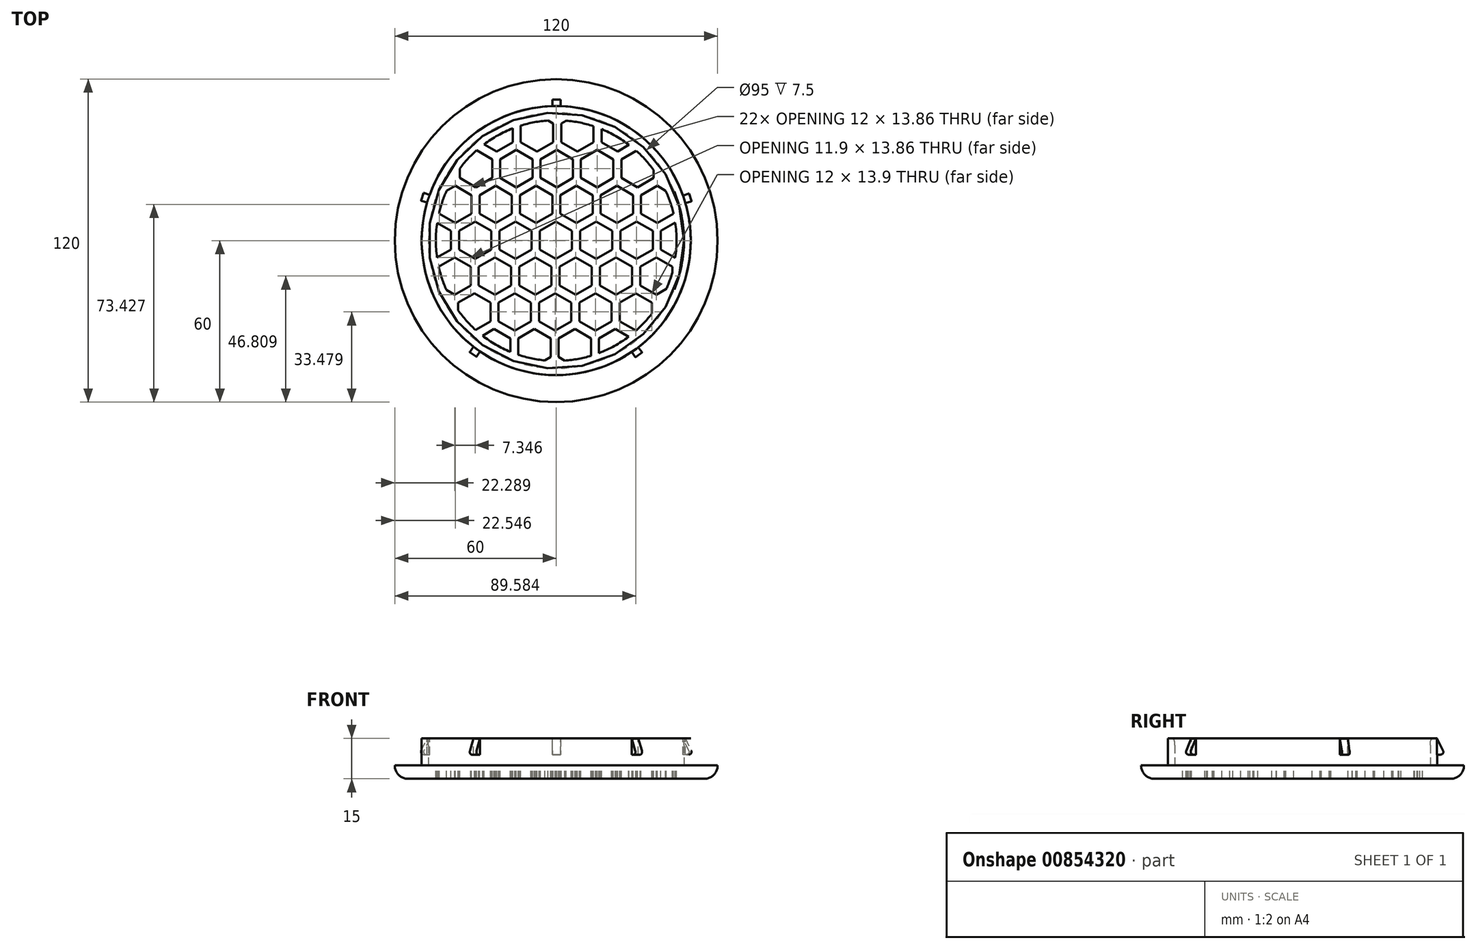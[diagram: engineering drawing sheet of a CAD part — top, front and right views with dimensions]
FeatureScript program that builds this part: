
annotation { "Feature Type Name" : "Feature", "Feature Type Description" : "" }
export const myFeature = defineFeature(function(context is Context, id is Id, definition is map)
    precondition{}
    {
        {
            var Q0;
            Q0=qCreatedBy(makeId("Top.planeOp"),FACE);
            var sketch = newSketch(context, id + "F0", { "sketchPlane" : qUnion([Q0])});
            skCircle(sketch, "E0", {"center": v(0, 0) * mm, "radius": 60 * mm});
            skSolve(sketch);
        }
        {
            var Q0;
            Q0 = qSketchRegion(id + "F0", true);
            extrude(context, id + "F1", {"entities" : qUnion([Q0]), "depth" : 5 * mm, "offsetDistance" : 25 * mm});
        }
        {
            var Q0;
            Q0=makeQuery(id+"F1.opExtrude","CAP_FACE",FACE,{"disambiguationData":[OSD([sQuery(id+"F0.wireOp",EDGE,"E0")])],"isStart":false});
            var sketch = newSketch(context, id + "F2", { "sketchPlane" : qUnion([Q0])});
            skLineSegment(sketch, "E1.0.3.0", {"start": v(-39.1, -3.35) * mm, "end": v(-44.27, -6.32) * mm});
            skLineSegment(sketch, "E1.0.3.4", {"start": v(-39.1, 3.58) * mm, "end": v(-39.1, -3.35) * mm});
            skLineSegment(sketch, "E1.0.3.5", {"start": v(-44.24, 6.54) * mm, "end": v(-39.1, 3.58) * mm});
            skLineSegment(sketch, "E1.0.4.0", {"start": v(-31.76, -16.66) * mm, "end": v(-37.76, -20.12) * mm});
            skLineSegment(sketch, "E1.0.4.2", {"start": v(-37.76, -20.12) * mm, "end": v(-40.76, -18.39) * mm});
            skLineSegment(sketch, "E1.0.4.3", {"start": v(-43.66, -9.67) * mm, "end": v(-37.76, -6.26) * mm});
            skLineSegment(sketch, "E1.0.4.4", {"start": v(-31.76, -9.73) * mm, "end": v(-31.76, -16.66) * mm});
            skLineSegment(sketch, "E1.0.4.5", {"start": v(-37.76, -6.26) * mm, "end": v(-31.76, -9.73) * mm});
            skLineSegment(sketch, "E1.0.5.0", {"start": v(-24.42, -29.96) * mm, "end": v(-29.98, -33.18) * mm});
            skLineSegment(sketch, "E1.0.5.1", {"start": v(-36.42, -25.95) * mm, "end": v(-36.42, -23.04) * mm});
            skLineSegment(sketch, "E1.0.5.3", {"start": v(-36.42, -23.04) * mm, "end": v(-30.42, -19.57) * mm});
            skLineSegment(sketch, "E1.0.5.4", {"start": v(-24.42, -23.04) * mm, "end": v(-24.42, -29.96) * mm});
            skLineSegment(sketch, "E1.0.5.5", {"start": v(-30.42, -19.57) * mm, "end": v(-24.42, -23.04) * mm});
            skLineSegment(sketch, "E1.0.6.3", {"start": v(-27.37, -35.36) * mm, "end": v(-23.07, -32.88) * mm});
            skLineSegment(sketch, "E1.0.6.4", {"start": v(-17.07, -36.35) * mm, "end": v(-17.07, -41.33) * mm});
            skLineSegment(sketch, "E1.0.6.5", {"start": v(-23.07, -32.88) * mm, "end": v(-17.07, -36.35) * mm});
            skLineSegment(sketch, "E1.1.2.0", {"start": v(-31.45, 9.96) * mm, "end": v(-37.45, 6.5) * mm});
            skLineSegment(sketch, "E1.1.2.1", {"start": v(-43.45, 9.96) * mm, "end": v(-43.45, 10.55) * mm});
            skLineSegment(sketch, "E1.1.2.2", {"start": v(-37.45, 6.5) * mm, "end": v(-43.45, 9.96) * mm});
            skLineSegment(sketch, "E1.1.2.3", {"start": v(-40.73, 18.47) * mm, "end": v(-37.45, 20.36) * mm});
            skLineSegment(sketch, "E1.1.2.4", {"start": v(-31.45, 16.9) * mm, "end": v(-31.45, 9.96) * mm});
            skLineSegment(sketch, "E1.1.2.5", {"start": v(-37.45, 20.36) * mm, "end": v(-31.45, 16.9) * mm});
            skLineSegment(sketch, "E1.1.3.0", {"start": v(-24.1, -3.35) * mm, "end": v(-30.1, -6.81) * mm});
            skLineSegment(sketch, "E1.1.3.1", {"start": v(-36.1, -3.35) * mm, "end": v(-36.1, 3.58) * mm});
            skLineSegment(sketch, "E1.1.3.2", {"start": v(-30.1, -6.81) * mm, "end": v(-36.1, -3.35) * mm});
            skLineSegment(sketch, "E1.1.3.3", {"start": v(-36.1, 3.58) * mm, "end": v(-30.1, 7.05) * mm});
            skLineSegment(sketch, "E1.1.3.4", {"start": v(-24.1, 3.58) * mm, "end": v(-24.1, -3.35) * mm});
            skLineSegment(sketch, "E1.1.3.5", {"start": v(-30.1, 7.05) * mm, "end": v(-24.1, 3.58) * mm});
            skLineSegment(sketch, "E1.1.4.0", {"start": v(-16.76, -16.66) * mm, "end": v(-22.76, -20.12) * mm});
            skLineSegment(sketch, "E1.1.4.1", {"start": v(-28.76, -16.66) * mm, "end": v(-28.76, -9.73) * mm});
            skLineSegment(sketch, "E1.1.4.2", {"start": v(-22.76, -20.12) * mm, "end": v(-28.76, -16.66) * mm});
            skLineSegment(sketch, "E1.1.4.3", {"start": v(-28.76, -9.73) * mm, "end": v(-22.76, -6.26) * mm});
            skLineSegment(sketch, "E1.1.4.4", {"start": v(-16.76, -9.73) * mm, "end": v(-16.76, -16.66) * mm});
            skLineSegment(sketch, "E1.1.4.5", {"start": v(-22.76, -6.26) * mm, "end": v(-16.76, -9.73) * mm});
            skLineSegment(sketch, "E1.1.5.0", {"start": v(-9.42, -29.96) * mm, "end": v(-15.42, -33.43) * mm});
            skLineSegment(sketch, "E1.1.5.1", {"start": v(-21.42, -29.96) * mm, "end": v(-21.42, -23.04) * mm});
            skLineSegment(sketch, "E1.1.5.2", {"start": v(-15.42, -33.43) * mm, "end": v(-21.42, -29.96) * mm});
            skLineSegment(sketch, "E1.1.5.3", {"start": v(-21.42, -23.04) * mm, "end": v(-15.42, -19.57) * mm});
            skLineSegment(sketch, "E1.1.5.4", {"start": v(-9.42, -23.04) * mm, "end": v(-9.42, -29.96) * mm});
            skLineSegment(sketch, "E1.1.5.5", {"start": v(-15.42, -19.57) * mm, "end": v(-9.42, -23.04) * mm});
            skLineSegment(sketch, "E1.1.6.0", {"start": v(-2.07, -43.27) * mm, "end": v(-4.22, -44.52) * mm});
            skLineSegment(sketch, "E1.1.6.1", {"start": v(-14.07, -42.45) * mm, "end": v(-14.07, -36.35) * mm});
            skLineSegment(sketch, "E1.1.6.3", {"start": v(-14.07, -36.35) * mm, "end": v(-8.07, -32.88) * mm});
            skLineSegment(sketch, "E1.1.6.4", {"start": v(-2.07, -36.35) * mm, "end": v(-2.07, -43.27) * mm});
            skLineSegment(sketch, "E1.1.6.5", {"start": v(-8.07, -32.88) * mm, "end": v(-2.07, -36.35) * mm});
            skLineSegment(sketch, "E1.2.1.0", {"start": v(-23.8, 23.27) * mm, "end": v(-29.8, 19.8) * mm});
            skLineSegment(sketch, "E1.2.1.1", {"start": v(-35.8, 23.27) * mm, "end": v(-35.8, 26.8) * mm});
            skLineSegment(sketch, "E1.2.1.2", {"start": v(-29.8, 19.8) * mm, "end": v(-35.8, 23.27) * mm});
            skLineSegment(sketch, "E1.2.1.4", {"start": v(-23.8, 30.2) * mm, "end": v(-23.8, 23.27) * mm});
            skLineSegment(sketch, "E1.2.1.5", {"start": v(-29.58, 33.54) * mm, "end": v(-23.8, 30.2) * mm});
            skLineSegment(sketch, "E1.2.2.0", {"start": v(-16.45, 9.96) * mm, "end": v(-22.45, 6.5) * mm});
            skLineSegment(sketch, "E1.2.2.1", {"start": v(-28.45, 9.96) * mm, "end": v(-28.45, 16.9) * mm});
            skLineSegment(sketch, "E1.2.2.2", {"start": v(-22.45, 6.5) * mm, "end": v(-28.45, 9.96) * mm});
            skLineSegment(sketch, "E1.2.2.3", {"start": v(-28.45, 16.9) * mm, "end": v(-22.45, 20.36) * mm});
            skLineSegment(sketch, "E1.2.2.4", {"start": v(-16.45, 16.9) * mm, "end": v(-16.45, 9.96) * mm});
            skLineSegment(sketch, "E1.2.2.5", {"start": v(-22.45, 20.36) * mm, "end": v(-16.45, 16.9) * mm});
            skLineSegment(sketch, "E1.2.3.0", {"start": v(-9.1, -3.35) * mm, "end": v(-15.1, -6.81) * mm});
            skLineSegment(sketch, "E1.2.3.1", {"start": v(-21.1, -3.35) * mm, "end": v(-21.1, 3.58) * mm});
            skLineSegment(sketch, "E1.2.3.2", {"start": v(-15.1, -6.81) * mm, "end": v(-21.1, -3.35) * mm});
            skLineSegment(sketch, "E1.2.3.3", {"start": v(-21.1, 3.58) * mm, "end": v(-15.1, 7.05) * mm});
            skLineSegment(sketch, "E1.2.3.4", {"start": v(-9.1, 3.58) * mm, "end": v(-9.1, -3.35) * mm});
            skLineSegment(sketch, "E1.2.3.5", {"start": v(-15.1, 7.05) * mm, "end": v(-9.1, 3.58) * mm});
            skLineSegment(sketch, "E1.2.4.0", {"start": v(-1.76, -16.66) * mm, "end": v(-7.76, -20.12) * mm});
            skLineSegment(sketch, "E1.2.4.1", {"start": v(-13.76, -16.66) * mm, "end": v(-13.76, -9.73) * mm});
            skLineSegment(sketch, "E1.2.4.2", {"start": v(-7.76, -20.12) * mm, "end": v(-13.76, -16.66) * mm});
            skLineSegment(sketch, "E1.2.4.3", {"start": v(-13.76, -9.73) * mm, "end": v(-7.76, -6.26) * mm});
            skLineSegment(sketch, "E1.2.4.4", {"start": v(-1.76, -9.73) * mm, "end": v(-1.76, -16.66) * mm});
            skLineSegment(sketch, "E1.2.4.5", {"start": v(-7.76, -6.26) * mm, "end": v(-1.76, -9.73) * mm});
            skLineSegment(sketch, "E1.2.5.0", {"start": v(5.58, -29.96) * mm, "end": v(-0.42, -33.43) * mm});
            skLineSegment(sketch, "E1.2.5.1", {"start": v(-6.42, -29.96) * mm, "end": v(-6.42, -23.04) * mm});
            skLineSegment(sketch, "E1.2.5.2", {"start": v(-0.42, -33.43) * mm, "end": v(-6.42, -29.96) * mm});
            skLineSegment(sketch, "E1.2.5.3", {"start": v(-6.42, -23.04) * mm, "end": v(-0.42, -19.57) * mm});
            skLineSegment(sketch, "E1.2.5.4", {"start": v(5.58, -23.04) * mm, "end": v(5.58, -29.96) * mm});
            skLineSegment(sketch, "E1.2.5.5", {"start": v(-0.42, -19.57) * mm, "end": v(5.58, -23.04) * mm});
            skLineSegment(sketch, "E1.2.6.1", {"start": v(0.93, -43.27) * mm, "end": v(0.93, -36.35) * mm});
            skLineSegment(sketch, "E1.2.6.2", {"start": v(3.23, -44.6) * mm, "end": v(0.93, -43.27) * mm});
            skLineSegment(sketch, "E1.2.6.3", {"start": v(0.93, -36.35) * mm, "end": v(6.93, -32.88) * mm});
            skLineSegment(sketch, "E1.2.6.4", {"start": v(12.93, -36.35) * mm, "end": v(12.93, -42.8) * mm});
            skLineSegment(sketch, "E1.2.6.5", {"start": v(6.93, -32.88) * mm, "end": v(12.93, -36.35) * mm});
            skLineSegment(sketch, "E1.3.0.0", {"start": v(-16.15, 36.58) * mm, "end": v(-22.15, 33.12) * mm});
            skLineSegment(sketch, "E1.3.0.2", {"start": v(-22.15, 33.12) * mm, "end": v(-26.8, 35.8) * mm});
            skLineSegment(sketch, "E1.3.0.4", {"start": v(-16.15, 41.7) * mm, "end": v(-16.15, 36.58) * mm});
            skLineSegment(sketch, "E1.3.1.0", {"start": v(-8.8, 23.27) * mm, "end": v(-14.8, 19.8) * mm});
            skLineSegment(sketch, "E1.3.1.1", {"start": v(-20.8, 23.27) * mm, "end": v(-20.8, 30.2) * mm});
            skLineSegment(sketch, "E1.3.1.2", {"start": v(-14.8, 19.8) * mm, "end": v(-20.8, 23.27) * mm});
            skLineSegment(sketch, "E1.3.1.3", {"start": v(-20.8, 30.2) * mm, "end": v(-14.8, 33.66) * mm});
            skLineSegment(sketch, "E1.3.1.4", {"start": v(-8.8, 30.2) * mm, "end": v(-8.8, 23.27) * mm});
            skLineSegment(sketch, "E1.3.1.5", {"start": v(-14.8, 33.66) * mm, "end": v(-8.8, 30.2) * mm});
            skLineSegment(sketch, "E1.3.2.0", {"start": v(-1.45, 9.96) * mm, "end": v(-7.45, 6.5) * mm});
            skLineSegment(sketch, "E1.3.2.1", {"start": v(-13.45, 9.96) * mm, "end": v(-13.45, 16.9) * mm});
            skLineSegment(sketch, "E1.3.2.2", {"start": v(-7.45, 6.5) * mm, "end": v(-13.45, 9.96) * mm});
            skLineSegment(sketch, "E1.3.2.3", {"start": v(-13.45, 16.9) * mm, "end": v(-7.45, 20.36) * mm});
            skLineSegment(sketch, "E1.3.2.4", {"start": v(-1.45, 16.9) * mm, "end": v(-1.45, 9.96) * mm});
            skLineSegment(sketch, "E1.3.2.5", {"start": v(-7.45, 20.36) * mm, "end": v(-1.45, 16.9) * mm});
            skLineSegment(sketch, "E1.3.3.0", {"start": v(5.9, -3.35) * mm, "end": v(-0.1, -6.81) * mm});
            skLineSegment(sketch, "E1.3.3.1", {"start": v(-6.1, -3.35) * mm, "end": v(-6.1, 3.58) * mm});
            skLineSegment(sketch, "E1.3.3.2", {"start": v(-0.1, -6.81) * mm, "end": v(-6.1, -3.35) * mm});
            skLineSegment(sketch, "E1.3.3.3", {"start": v(-6.1, 3.58) * mm, "end": v(-0.1, 7.05) * mm});
            skLineSegment(sketch, "E1.3.3.4", {"start": v(5.9, 3.58) * mm, "end": v(5.9, -3.35) * mm});
            skLineSegment(sketch, "E1.3.3.5", {"start": v(-0.1, 7.05) * mm, "end": v(5.9, 3.58) * mm});
            skLineSegment(sketch, "E1.3.4.0", {"start": v(13.24, -16.66) * mm, "end": v(7.24, -20.12) * mm});
            skLineSegment(sketch, "E1.3.4.1", {"start": v(1.24, -16.66) * mm, "end": v(1.24, -9.73) * mm});
            skLineSegment(sketch, "E1.3.4.2", {"start": v(7.24, -20.12) * mm, "end": v(1.24, -16.66) * mm});
            skLineSegment(sketch, "E1.3.4.3", {"start": v(1.24, -9.73) * mm, "end": v(7.24, -6.26) * mm});
            skLineSegment(sketch, "E1.3.4.4", {"start": v(13.24, -9.73) * mm, "end": v(13.24, -16.66) * mm});
            skLineSegment(sketch, "E1.3.4.5", {"start": v(7.24, -6.26) * mm, "end": v(13.24, -9.73) * mm});
            skLineSegment(sketch, "E1.3.5.0", {"start": v(20.58, -29.96) * mm, "end": v(14.58, -33.43) * mm});
            skLineSegment(sketch, "E1.3.5.1", {"start": v(8.58, -29.96) * mm, "end": v(8.58, -23.04) * mm});
            skLineSegment(sketch, "E1.3.5.2", {"start": v(14.58, -33.43) * mm, "end": v(8.58, -29.96) * mm});
            skLineSegment(sketch, "E1.3.5.3", {"start": v(8.58, -23.04) * mm, "end": v(14.58, -19.57) * mm});
            skLineSegment(sketch, "E1.3.5.4", {"start": v(20.58, -23.04) * mm, "end": v(20.58, -29.96) * mm});
            skLineSegment(sketch, "E1.3.5.5", {"start": v(14.58, -19.57) * mm, "end": v(20.58, -23.04) * mm});
            skLineSegment(sketch, "E1.3.6.1", {"start": v(15.93, -41.78) * mm, "end": v(15.93, -36.35) * mm});
            skLineSegment(sketch, "E1.3.6.3", {"start": v(15.93, -36.35) * mm, "end": v(21.93, -32.88) * mm});
            skLineSegment(sketch, "E1.3.6.5", {"start": v(21.93, -32.88) * mm, "end": v(26.88, -35.74) * mm});
            skLineSegment(sketch, "E1.4.0.0", {"start": v(-1.15, 36.58) * mm, "end": v(-7.15, 33.12) * mm});
            skLineSegment(sketch, "E1.4.0.1", {"start": v(-13.15, 36.58) * mm, "end": v(-13.15, 42.74) * mm});
            skLineSegment(sketch, "E1.4.0.2", {"start": v(-7.15, 33.12) * mm, "end": v(-13.15, 36.58) * mm});
            skLineSegment(sketch, "E1.4.0.4", {"start": v(-1.15, 43.51) * mm, "end": v(-1.15, 36.58) * mm});
            skLineSegment(sketch, "E1.4.0.5", {"start": v(-3.05, 44.61) * mm, "end": v(-1.15, 43.51) * mm});
            skLineSegment(sketch, "E1.4.1.0", {"start": v(6.2, 23.27) * mm, "end": v(0.2, 19.8) * mm});
            skLineSegment(sketch, "E1.4.1.1", {"start": v(-5.8, 23.27) * mm, "end": v(-5.8, 30.2) * mm});
            skLineSegment(sketch, "E1.4.1.2", {"start": v(0.2, 19.8) * mm, "end": v(-5.8, 23.27) * mm});
            skLineSegment(sketch, "E1.4.1.3", {"start": v(-5.8, 30.2) * mm, "end": v(0.2, 33.66) * mm});
            skLineSegment(sketch, "E1.4.1.4", {"start": v(6.2, 30.2) * mm, "end": v(6.2, 23.27) * mm});
            skLineSegment(sketch, "E1.4.1.5", {"start": v(0.2, 33.66) * mm, "end": v(6.2, 30.2) * mm});
            skLineSegment(sketch, "E1.4.2.0", {"start": v(13.55, 9.96) * mm, "end": v(7.55, 6.5) * mm});
            skLineSegment(sketch, "E1.4.2.1", {"start": v(1.55, 9.96) * mm, "end": v(1.55, 16.9) * mm});
            skLineSegment(sketch, "E1.4.2.2", {"start": v(7.55, 6.5) * mm, "end": v(1.55, 9.96) * mm});
            skLineSegment(sketch, "E1.4.2.3", {"start": v(1.55, 16.9) * mm, "end": v(7.55, 20.36) * mm});
            skLineSegment(sketch, "E1.4.2.4", {"start": v(13.55, 16.9) * mm, "end": v(13.55, 9.96) * mm});
            skLineSegment(sketch, "E1.4.2.5", {"start": v(7.55, 20.36) * mm, "end": v(13.55, 16.9) * mm});
            skLineSegment(sketch, "E1.4.3.0", {"start": v(20.9, -3.35) * mm, "end": v(14.9, -6.81) * mm});
            skLineSegment(sketch, "E1.4.3.1", {"start": v(8.9, -3.35) * mm, "end": v(8.9, 3.58) * mm});
            skLineSegment(sketch, "E1.4.3.2", {"start": v(14.9, -6.81) * mm, "end": v(8.9, -3.35) * mm});
            skLineSegment(sketch, "E1.4.3.3", {"start": v(8.9, 3.58) * mm, "end": v(14.9, 7.05) * mm});
            skLineSegment(sketch, "E1.4.3.4", {"start": v(20.9, 3.58) * mm, "end": v(20.9, -3.35) * mm});
            skLineSegment(sketch, "E1.4.3.5", {"start": v(14.9, 7.05) * mm, "end": v(20.9, 3.58) * mm});
            skLineSegment(sketch, "E1.4.4.0", {"start": v(28.24, -16.66) * mm, "end": v(22.24, -20.12) * mm});
            skLineSegment(sketch, "E1.4.4.1", {"start": v(16.24, -16.66) * mm, "end": v(16.24, -9.73) * mm});
            skLineSegment(sketch, "E1.4.4.2", {"start": v(22.24, -20.12) * mm, "end": v(16.24, -16.66) * mm});
            skLineSegment(sketch, "E1.4.4.3", {"start": v(16.24, -9.73) * mm, "end": v(22.24, -6.26) * mm});
            skLineSegment(sketch, "E1.4.4.4", {"start": v(28.24, -9.73) * mm, "end": v(28.24, -16.66) * mm});
            skLineSegment(sketch, "E1.4.4.5", {"start": v(22.24, -6.26) * mm, "end": v(28.24, -9.73) * mm});
            skLineSegment(sketch, "E1.4.5.1", {"start": v(23.58, -29.96) * mm, "end": v(23.58, -23.04) * mm});
            skLineSegment(sketch, "E1.4.5.2", {"start": v(29.96, -33.65) * mm, "end": v(23.58, -29.96) * mm});
            skLineSegment(sketch, "E1.4.5.3", {"start": v(23.58, -23.04) * mm, "end": v(29.58, -19.57) * mm});
            skLineSegment(sketch, "E1.4.5.4", {"start": v(35.58, -23.04) * mm, "end": v(35.58, -27.08) * mm});
            skLineSegment(sketch, "E1.4.5.5", {"start": v(29.58, -19.57) * mm, "end": v(35.58, -23.04) * mm});
            skLineSegment(sketch, "E1.5.0.0", {"start": v(13.85, 36.58) * mm, "end": v(7.85, 33.12) * mm});
            skLineSegment(sketch, "E1.5.0.1", {"start": v(1.85, 36.58) * mm, "end": v(1.85, 43.51) * mm});
            skLineSegment(sketch, "E1.5.0.2", {"start": v(7.85, 33.12) * mm, "end": v(1.85, 36.58) * mm});
            skLineSegment(sketch, "E1.5.0.3", {"start": v(1.85, 43.51) * mm, "end": v(3.68, 44.56) * mm});
            skLineSegment(sketch, "E1.5.0.4", {"start": v(13.85, 42.52) * mm, "end": v(13.85, 36.58) * mm});
            skLineSegment(sketch, "E1.5.1.0", {"start": v(21.2, 23.27) * mm, "end": v(15.2, 19.8) * mm});
            skLineSegment(sketch, "E1.5.1.1", {"start": v(9.2, 23.27) * mm, "end": v(9.2, 30.2) * mm});
            skLineSegment(sketch, "E1.5.1.2", {"start": v(15.2, 19.8) * mm, "end": v(9.2, 23.27) * mm});
            skLineSegment(sketch, "E1.5.1.3", {"start": v(9.2, 30.2) * mm, "end": v(15.2, 33.66) * mm});
            skLineSegment(sketch, "E1.5.1.4", {"start": v(21.2, 30.2) * mm, "end": v(21.2, 23.27) * mm});
            skLineSegment(sketch, "E1.5.1.5", {"start": v(15.2, 33.66) * mm, "end": v(21.2, 30.2) * mm});
            skLineSegment(sketch, "E1.5.2.0", {"start": v(28.55, 9.96) * mm, "end": v(22.55, 6.5) * mm});
            skLineSegment(sketch, "E1.5.2.1", {"start": v(16.55, 9.96) * mm, "end": v(16.55, 16.9) * mm});
            skLineSegment(sketch, "E1.5.2.2", {"start": v(22.55, 6.5) * mm, "end": v(16.55, 9.96) * mm});
            skLineSegment(sketch, "E1.5.2.3", {"start": v(16.55, 16.9) * mm, "end": v(22.55, 20.36) * mm});
            skLineSegment(sketch, "E1.5.2.4", {"start": v(28.55, 16.9) * mm, "end": v(28.55, 9.96) * mm});
            skLineSegment(sketch, "E1.5.2.5", {"start": v(22.55, 20.36) * mm, "end": v(28.55, 16.9) * mm});
            skLineSegment(sketch, "E1.5.3.0", {"start": v(35.9, -3.35) * mm, "end": v(29.9, -6.81) * mm});
            skLineSegment(sketch, "E1.5.3.1", {"start": v(23.9, -3.35) * mm, "end": v(23.9, 3.58) * mm});
            skLineSegment(sketch, "E1.5.3.2", {"start": v(29.9, -6.81) * mm, "end": v(23.9, -3.35) * mm});
            skLineSegment(sketch, "E1.5.3.3", {"start": v(23.9, 3.58) * mm, "end": v(29.9, 7.05) * mm});
            skLineSegment(sketch, "E1.5.3.4", {"start": v(35.9, 3.58) * mm, "end": v(35.9, -3.35) * mm});
            skLineSegment(sketch, "E1.5.3.5", {"start": v(29.9, 7.05) * mm, "end": v(35.9, 3.58) * mm});
            skLineSegment(sketch, "E1.5.4.0", {"start": v(40.94, -17.98) * mm, "end": v(37.24, -20.12) * mm});
            skLineSegment(sketch, "E1.5.4.1", {"start": v(31.24, -16.66) * mm, "end": v(31.24, -9.73) * mm});
            skLineSegment(sketch, "E1.5.4.2", {"start": v(37.24, -20.12) * mm, "end": v(31.24, -16.66) * mm});
            skLineSegment(sketch, "E1.5.4.3", {"start": v(31.24, -9.73) * mm, "end": v(37.24, -6.26) * mm});
            skLineSegment(sketch, "E1.5.4.4", {"start": v(43.24, -9.73) * mm, "end": v(43.24, -11.4) * mm});
            skLineSegment(sketch, "E1.5.4.5", {"start": v(37.24, -6.26) * mm, "end": v(43.24, -9.73) * mm});
            skLineSegment(sketch, "E1.6.0.0", {"start": v(27.1, 35.57) * mm, "end": v(22.85, 33.12) * mm});
            skLineSegment(sketch, "E1.6.0.1", {"start": v(16.85, 36.58) * mm, "end": v(16.85, 41.42) * mm});
            skLineSegment(sketch, "E1.6.0.2", {"start": v(22.85, 33.12) * mm, "end": v(16.85, 36.58) * mm});
            skLineSegment(sketch, "E1.6.1.0", {"start": v(36.2, 23.27) * mm, "end": v(30.2, 19.8) * mm});
            skLineSegment(sketch, "E1.6.1.1", {"start": v(24.2, 23.27) * mm, "end": v(24.2, 30.2) * mm});
            skLineSegment(sketch, "E1.6.1.2", {"start": v(30.2, 19.8) * mm, "end": v(24.2, 23.27) * mm});
            skLineSegment(sketch, "E1.6.1.3", {"start": v(24.2, 30.2) * mm, "end": v(29.74, 33.4) * mm});
            skLineSegment(sketch, "E1.6.1.4", {"start": v(36.2, 26.25) * mm, "end": v(36.2, 23.27) * mm});
            skLineSegment(sketch, "E1.6.2.0", {"start": v(43.55, 9.96) * mm, "end": v(37.55, 6.5) * mm});
            skLineSegment(sketch, "E1.6.2.1", {"start": v(31.55, 9.96) * mm, "end": v(31.55, 16.9) * mm});
            skLineSegment(sketch, "E1.6.2.2", {"start": v(37.55, 6.5) * mm, "end": v(31.55, 9.96) * mm});
            skLineSegment(sketch, "E1.6.2.3", {"start": v(31.55, 16.9) * mm, "end": v(37.55, 20.36) * mm});
            skLineSegment(sketch, "E1.6.2.4", {"start": v(43.55, 10.16) * mm, "end": v(43.55, 9.96) * mm});
            skLineSegment(sketch, "E1.6.2.5", {"start": v(37.55, 20.36) * mm, "end": v(40.7, 18.54) * mm});
            skLineSegment(sketch, "E1.6.3.1", {"start": v(38.9, -3.35) * mm, "end": v(38.9, 3.58) * mm});
            skLineSegment(sketch, "E1.6.3.2", {"start": v(44.25, -6.44) * mm, "end": v(38.9, -3.35) * mm});
            skLineSegment(sketch, "E1.6.3.3", {"start": v(38.9, 3.58) * mm, "end": v(44.22, 6.66) * mm});
            skArc(sketch, "E2", {"start": v(-3.05, 44.61) * mm, "mid": v(-8.15, 43.97) * mm, "end": v(-13.15, 42.74) * mm});
            skArc(sketch, "E3.trimOffspring", {"start": v(-16.15, 41.7) * mm, "mid": v(-21.67, 39.11) * mm, "end": v(-26.8, 35.8) * mm});
            skArc(sketch, "E4.trimOffspring", {"start": v(19.6, 40.19) * mm, "mid": v(18.24, 40.83) * mm, "end": v(16.85, 41.42) * mm});
            skArc(sketch, "E5.trimOffspring", {"start": v(27.1, 35.57) * mm, "mid": v(22.17, 38.83) * mm, "end": v(16.85, 41.42) * mm});
            skArc(sketch, "E6.trimOffspring", {"start": v(36.2, 26.25) * mm, "mid": v(33.16, 30) * mm, "end": v(29.74, 33.4) * mm});
            skArc(sketch, "E7.trimOffspring", {"start": v(43.55, 10.16) * mm, "mid": v(42.33, 14.42) * mm, "end": v(40.7, 18.54) * mm});
            skArc(sketch, "E8.trimOffspring", {"start": v(44.25, -6.44) * mm, "mid": v(44.72, 0.1) * mm, "end": v(44.22, 6.66) * mm});
            skArc(sketch, "E9.trimOffspring", {"start": v(40.94, -17.98) * mm, "mid": v(42.22, -14.74) * mm, "end": v(43.24, -11.4) * mm});
            skArc(sketch, "E10.trimOffspring", {"start": v(29.65, -33.47) * mm, "mid": v(32.77, -30.42) * mm, "end": v(35.58, -27.08) * mm});
            skArc(sketch, "E11.trimOffspring", {"start": v(15.93, -41.78) * mm, "mid": v(21.62, -39.14) * mm, "end": v(26.88, -35.74) * mm});
            skArc(sketch, "E12.trimOffspring", {"start": v(3.23, -44.6) * mm, "mid": v(8.13, -43.97) * mm, "end": v(12.93, -42.8) * mm});
            skArc(sketch, "E13.trimOffspring", {"start": v(-14.07, -42.45) * mm, "mid": v(-9.2, -43.76) * mm, "end": v(-4.22, -44.52) * mm});
            skArc(sketch, "E14.trimOffspring", {"start": v(-27.37, -35.36) * mm, "mid": v(-22.42, -38.7) * mm, "end": v(-17.07, -41.33) * mm});
            skArc(sketch, "E15.trimOffspring", {"start": v(-36.42, -25.95) * mm, "mid": v(-33.4, -29.74) * mm, "end": v(-29.98, -33.18) * mm});
            skArc(sketch, "E16.trimOffspring", {"start": v(-43.66, -9.67) * mm, "mid": v(-42.43, -14.1) * mm, "end": v(-40.76, -18.39) * mm});
            skArc(sketch, "E17.trimOffspring", {"start": v(-44.24, 6.54) * mm, "mid": v(-44.72, 0.1) * mm, "end": v(-44.27, -6.32) * mm});
            skArc(sketch, "E18.trimOffspring", {"start": v(-40.73, 18.47) * mm, "mid": v(-42.28, 14.57) * mm, "end": v(-43.45, 10.55) * mm});
            skArc(sketch, "E19.trimOffspring", {"start": v(-29.58, 33.54) * mm, "mid": v(-32.86, 30.33) * mm, "end": v(-35.8, 26.8) * mm});
            skArc(sketch, "E20.trimOffspring", {"start": v(-16.15, 41.7) * mm, "mid": v(-16.36, 41.62) * mm, "end": v(-16.57, 41.53) * mm});
            skArc(sketch, "E21.trimOffspring", {"start": v(13.85, 42.52) * mm, "mid": v(8.83, 43.84) * mm, "end": v(3.68, 44.56) * mm});
            skSolve(sketch);
        }
        {
            var Q0;
            Q0 = qSketchRegion(id + "F2", true);
            extrude(context, id + "F3", {"entities" : qUnion([Q0]), "operationType" : NewBodyOperationType.REMOVE, "endBound" : BoundingType.THROUGH_ALL, "oppositeDirection" : true, "depth" : 25 * mm, "offsetDistance" : 25 * mm});
        }
        {
            var Q0;
            Q0=makeQuery(id+"F1.opExtrude","CAP_FACE",FACE,{"disambiguationData":[OSD([sQuery(id+"F0.wireOp",EDGE,"E0")])],"isStart":false});
            var sketch = newSketch(context, id + "F4", { "sketchPlane" : qUnion([Q0])});
            skCircle(sketch, "E22", {"center": v(0, 0) * mm, "radius": 50 * mm});
            skCircle(sketch, "E23", {"center": v(0, 0) * mm, "radius": 47.5 * mm});
            skSolve(sketch);
        }
        {
            var Q0;
            Q0 = qSketchRegion(id + "F4", true);
            extrude(context, id + "F5", {"entities" : qUnion([Q0]), "operationType" : NewBodyOperationType.ADD, "depth" : 10 * mm, "offsetDistance" : 25 * mm});
        }
        {
            var Q0;
            Q0=makeQuery(id+"F5.opExtrude","CAP_FACE",FACE,{"disambiguationData":[OSD([sQuery(id+"F4.wireOp",EDGE,"E22"),sQuery(id+"F4.wireOp",EDGE,"E23")])],"isStart":false});
            var sketch = newSketch(context, id + "F6", { "sketchPlane" : qUnion([Q0])});
            skLineSegment(sketch, "E24.bottom", {"start": v(-1.38, 52.97) * mm, "end": v(1.62, 52.97) * mm});
            skLineSegment(sketch, "E24.left", {"start": v(-1.38, 52.97) * mm, "end": v(-1.38, 49.98) * mm});
            skLineSegment(sketch, "E24.right", {"start": v(1.62, 52.97) * mm, "end": v(1.62, 49.97) * mm});
            skArc(sketch, "E25.0", {"start": v(1.62, 49.97) * mm, "mid": v(0.12, 50) * mm, "end": v(-1.38, 49.98) * mm});
            skSolve(sketch);
        }
        {
            var Q0;
            Q0 = qSketchRegion(id + "F6", true);
            extrude(context, id + "F7", {"entities" : qUnion([Q0]), "oppositeDirection" : true, "depth" : 6 * mm, "offsetDistance" : 25 * mm});
        }
        {
            var Q0;
            Q0=makeQuery(id+"F7.opExtrude","SWEPT_FACE",FACE,{"disambiguationData":[OSD([sQuery(id+"F6.wireOp",EDGE,"E24.right")])]});
            var sketch = newSketch(context, id + "F8", { "sketchPlane" : qUnion([Q0])});
            skLineSegment(sketch, "E26", {"start": v(49.97, 15) * mm, "end": v(52.97, 9) * mm});
            skLineSegment(sketch, "E27", {"start": v(52.97, 9) * mm, "end": v(52.97, 15) * mm});
            skLineSegment(sketch, "E28", {"start": v(52.97, 15) * mm, "end": v(49.97, 15) * mm});
            skSolve(sketch);
        }
        {
            var Q0;
            Q0 = qSketchRegion(id + "F8", true);
            extrude(context, id + "F9", {"entities" : qUnion([Q0]), "operationType" : NewBodyOperationType.REMOVE, "oppositeDirection" : true, "depth" : 25 * mm, "offsetDistance" : 25 * mm});
        }
        {
            var Q0;
            Q0=makeQuery(id+"F9.boolean.opBoolean","MERGE",EDGE,{"derivedFrom":[makeQuery(id+"F7.opExtrude","CAP_EDGE",EDGE,{"disambiguationData":[OSD([sQuery(id+"F6.wireOp",EDGE,"E24.bottom")])],"isStart":false})],"fromTools":[makeQuery(id+"F9.opExtrude","SWEPT_EDGE",EDGE,{"disambiguationData":[OSD([sQuery(id+"F6.wireOp",EDGE,"E24.right"),sQuery(id+"F8.wireOp",EDGE,"E26"),sQuery(id+"F8.wireOp",EDGE,"E27")])]})]});
            fillet(context, id + "F10", {"entities" : qUnion([Q0]), "radius" : 1 * mm, "tangentPropagation" : true, "allowEdgeOverflow" : false});
        }
        {
            var Q0;
            Q0=qCreatedBy(makeId("Front.planeOp"),FACE);
            var sketch = newSketch(context, id + "F11", { "sketchPlane" : qUnion([Q0])});
            skLineSegment(sketch, "E29", {"start": v(0, -18.33) * mm, "end": v(0, 29.72) * mm, "construction": true});
            skSolve(sketch);
        }
        {
            var Q0;
            Q0=makeQuery(id+"F7.opExtrude","SWEPT_BODY",BODY,{"disambiguationData":[OSD([sQuery(id+"F6.wireOp",EDGE,"E24.bottom"),sQuery(id+"F6.wireOp",EDGE,"E24.left"),sQuery(id+"F6.wireOp",EDGE,"E24.right"),sQuery(id+"F6.wireOp",EDGE,"E25.0")])]});
            var Q1;
            Q1=sQuery(id+"F11.wireOp",EDGE,"E29");
            circularPattern(context, id + "F12", {"operationType" : NewBodyOperationType.ADD, "entities" : qUnion([Q0]), "axis" : qUnion([Q1]), "angle" : 360 * degree, "instanceCount" : 5, "equalSpace" : true});
        }
        {
            var Q0;
            Q0=makeQuery(id+"F1.opExtrude","CAP_EDGE",EDGE,{"disambiguationData":[OSD([sQuery(id+"F0.wireOp",EDGE,"E0")])],"isStart":true});
            fillet(context, id + "F13", {"entities" : qUnion([Q0]), "radius" : 5 * mm, "tangentPropagation" : true, "allowEdgeOverflow" : false});
        }
        {
            var Q0;
            Q0=makeQuery(id+"F5.opExtrude","CAP_EDGE",EDGE,{"disambiguationData":[OSD([sQuery(id+"F4.wireOp",EDGE,"E23")])],"isStart":false});
            fillet(context, id + "F14", {"entities" : qUnion([Q0]), "radius" : 2.5 * mm, "tangentPropagation" : true, "rho" : 0.7, "crossSection" : FilletCrossSection.CONIC, "allowEdgeOverflow" : false});
        }
    });
